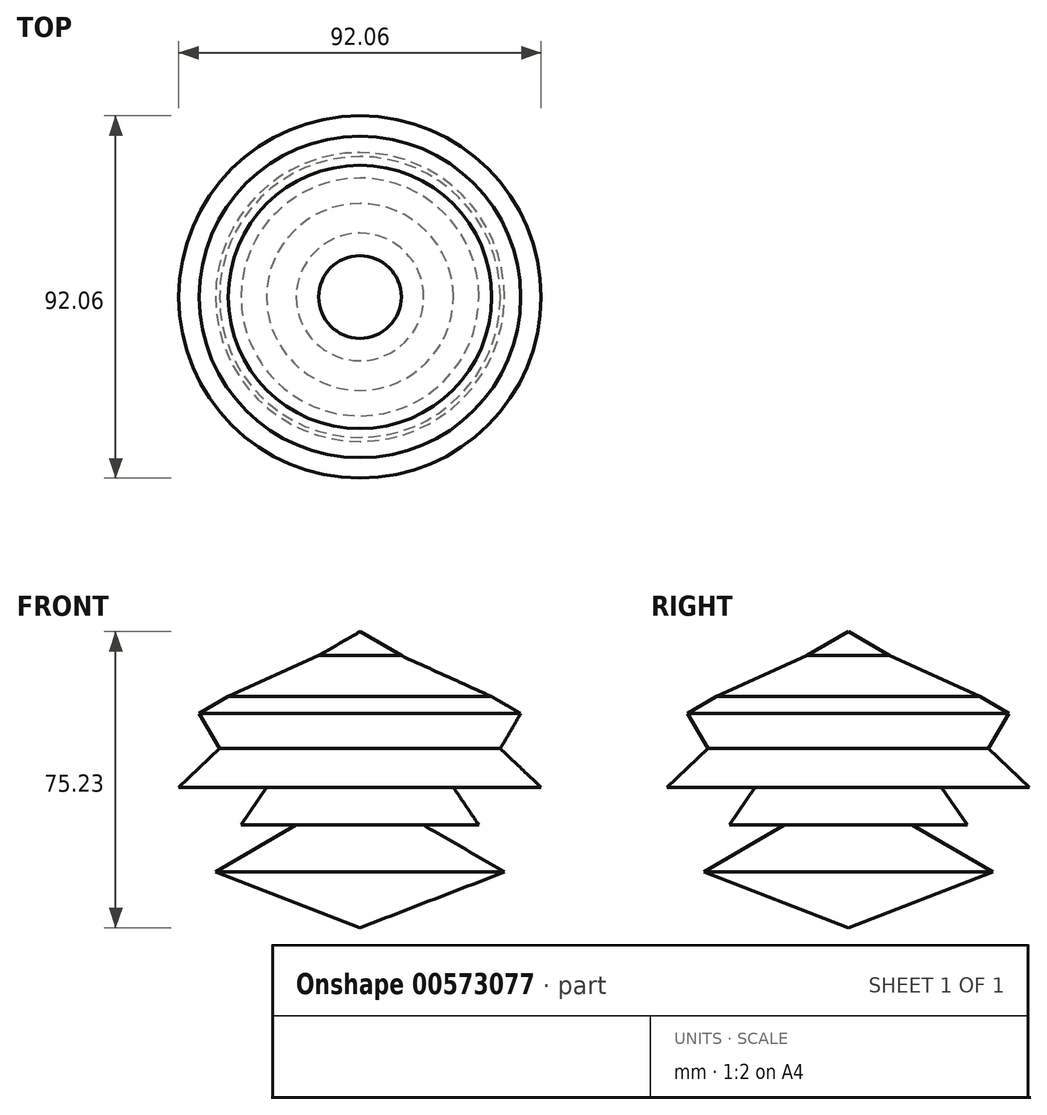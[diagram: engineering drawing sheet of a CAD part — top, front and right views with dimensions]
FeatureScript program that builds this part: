
annotation { "Feature Type Name" : "Feature", "Feature Type Description" : "" }
export const myFeature = defineFeature(function(context is Context, id is Id, definition is map)
    precondition{}
    {
        {
            var Q0;
            Q0=qCreatedBy(makeId("Front.planeOp"),FACE);
            var sketch = newSketch(context, id + "F0", { "sketchPlane" : qUnion([Q0])});
            skLineSegment(sketch, "E0", {"start": v(0, 0) * mm, "end": v(-36.7, 14.13) * mm});
            skLineSegment(sketch, "E1", {"start": v(-36.7, 14.13) * mm, "end": v(-16.2, 26.06) * mm});
            skLineSegment(sketch, "E2", {"start": v(-16.2, 26.06) * mm, "end": v(-30.21, 26.06) * mm});
            skLineSegment(sketch, "E3", {"start": v(-30.21, 26.06) * mm, "end": v(-23.73, 35.66) * mm});
            skLineSegment(sketch, "E4", {"start": v(-23.73, 35.66) * mm, "end": v(-46.03, 35.66) * mm});
            skLineSegment(sketch, "E5", {"start": v(-46.03, 35.66) * mm, "end": v(-35.66, 45.52) * mm});
            skLineSegment(sketch, "E6", {"start": v(-35.66, 45.52) * mm, "end": v(-40.85, 54.42) * mm});
            skPoint(sketch, "E6.endSnap0", {"position": v(-40.85, 40.59) * mm});
            skLineSegment(sketch, "E7", {"start": v(-40.85, 54.42) * mm, "end": v(-33.47, 58.72) * mm});
            skLineSegment(sketch, "E8", {"start": v(-33.47, 58.72) * mm, "end": v(-10.5, 69.12) * mm});
            skLineSegment(sketch, "E9", {"start": v(-10.5, 69.12) * mm, "end": v(0, 75.23) * mm});
            skLineSegment(sketch, "E10", {"start": v(0, 75.23) * mm, "end": v(0, 0) * mm});
            skSolve(sketch);
        }
        {
            var Q0;
            Q0=makeQuery(id+"F0.imprint","IMPRINT",FACE,{"disambiguationData":[TD([[makeQuery(id+"F0.imprint","IMPRINT",EDGE,{"derivedFrom":sQuery(id+"F0.wireOp",EDGE,"E0")}),-1.0]])]});
            var Q1;
            Q1=sQuery(id+"F0.wireOp",EDGE,"E10");
            revolve(context, id + "F1", {"entities" : qUnion([Q0]), "axis" : qUnion([Q1]), "revolveType" : RevolveType.FULL});
        }
    });
